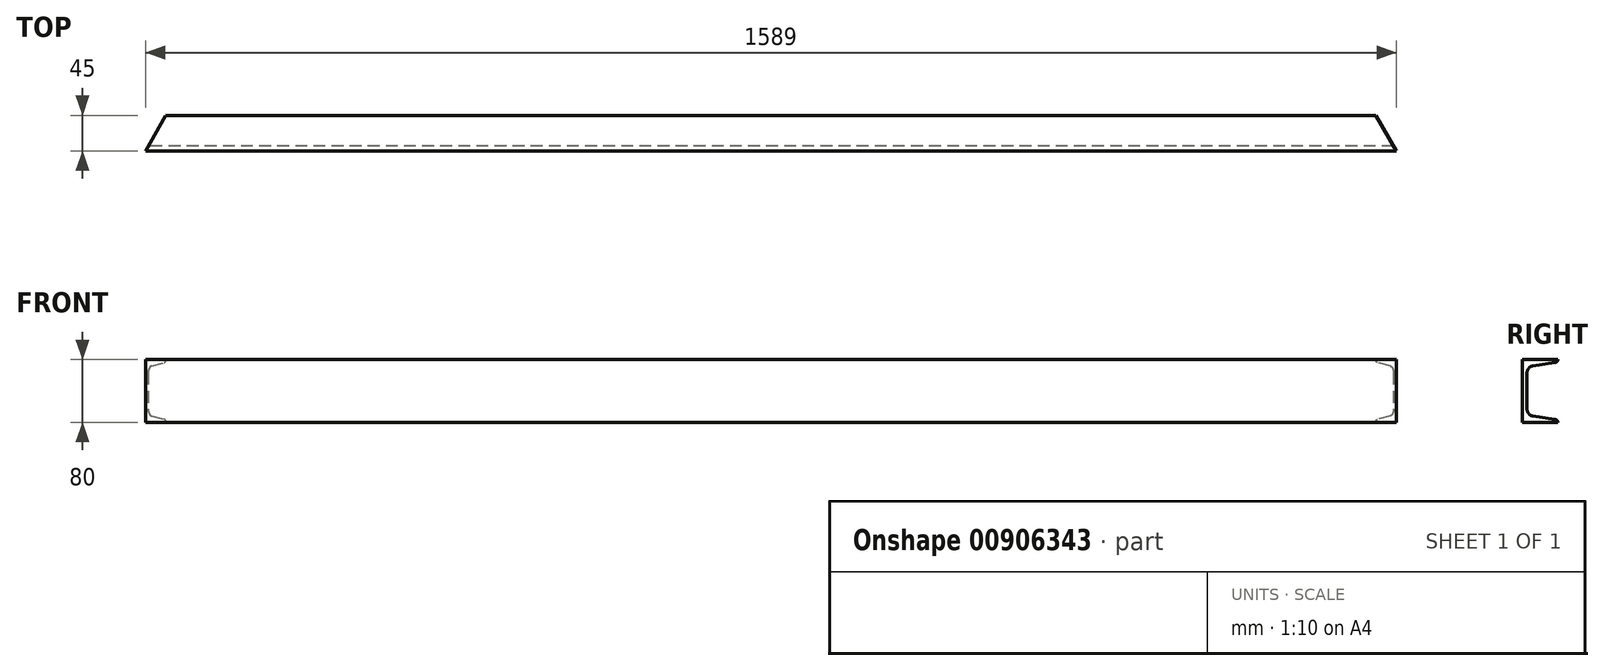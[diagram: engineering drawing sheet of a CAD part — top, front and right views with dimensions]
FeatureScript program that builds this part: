
annotation { "Feature Type Name" : "Feature", "Feature Type Description" : "" }
export const myFeature = defineFeature(function(context is Context, id is Id, definition is map)
    precondition{}
    {
        {
            var Q0;
            Q0=qCreatedBy(makeId("Top.planeOp"),FACE);
            var sketch = newSketch(context, id + "F0", { "sketchPlane" : qUnion([Q0])});
            skLineSegment(sketch, "E0", {"start": v(-794.5, 0) * mm, "end": v(794.5, 0) * mm});
            skLineSegment(sketch, "E1", {"start": v(794.5, 0) * mm, "end": v(768.52, 45) * mm});
            skLineSegment(sketch, "E2", {"start": v(768.52, 45) * mm, "end": v(-768.52, 45) * mm});
            skLineSegment(sketch, "E3", {"start": v(-768.52, 45) * mm, "end": v(-794.5, 0) * mm});
            skLineSegment(sketch, "E4", {"start": v(0, 220.63) * mm, "end": v(0, 0) * mm, "construction": true});
            skSolve(sketch);
        }
        {
            var Q0;
            Q0=qCreatedBy(makeId("Right.planeOp"),FACE);
            var sketch = newSketch(context, id + "F1", { "sketchPlane" : qUnion([Q0])});
            skLineSegment(sketch, "E5", {"start": v(0, 40) * mm, "end": v(0, 80) * mm});
            skLineSegment(sketch, "E6", {"start": v(0, 80) * mm, "end": v(45, 80) * mm});
            skPoint(sketch, "E7.startSnap0", {"position": v(0, 40) * mm});
            skLineSegment(sketch, "E8", {"start": v(0, 40) * mm, "end": v(15, 40) * mm});
            skLineSegment(sketch, "E9", {"start": v(15, 40) * mm, "end": v(15, 63) * mm, "construction": true});
            skLineSegment(sketch, "E10", {"start": v(15, 40) * mm, "end": v(15, 17) * mm, "construction": true});
            skLineSegment(sketch, "E11", {"start": v(6, 63) * mm, "end": v(6, 40) * mm});
            skArc(sketch, "E12", {"start": v(13.68, 71.9) * mm, "mid": v(8.19, 68.88) * mm, "end": v(6, 63) * mm});
            skArc(sketch, "E13", {"start": v(41.59, 76.04) * mm, "mid": v(44.03, 77.39) * mm, "end": v(45, 80) * mm});
            skLineSegment(sketch, "E14", {"start": v(13.68, 71.9) * mm, "end": v(41.59, 76.04) * mm});
            skArc(sketch, "E15.MirrorCS", {"start": v(13.68, 8.1) * mm, "mid": v(8.19, 11.12) * mm, "end": v(6, 17) * mm});
            skLineSegment(sketch, "E16.MirrorCS", {"start": v(0, 40) * mm, "end": v(0, 0) * mm});
            skLineSegment(sketch, "E17.MirrorCS", {"start": v(0, 0) * mm, "end": v(45, 0) * mm});
            skLineSegment(sketch, "E18.MirrorCS", {"start": v(6, 17) * mm, "end": v(6, 40) * mm});
            skArc(sketch, "E19.MirrorCS", {"start": v(41.59, 3.96) * mm, "mid": v(44.03, 2.61) * mm, "end": v(45, 0) * mm});
            skLineSegment(sketch, "E20.MirrorCS", {"start": v(13.68, 8.1) * mm, "end": v(41.59, 3.96) * mm});
            skSolve(sketch);
        }
        {
            var Q0;
            Q0 = qSketchRegion(id + "F1", true);
            extrude(context, id + "F2", {"entities" : qUnion([Q0]), "endBound" : BoundingType.SYMMETRIC, "depth" : 1589 * mm, "offsetDistance" : 25 * mm});
        }
        {
            var Q0;
            Q0=makeQuery(id+"F2.opExtrude","SWEPT_FACE",FACE,{"disambiguationData":[OSD([sQuery(id+"F1.wireOp",EDGE,"E6")])]});
            var sketch = newSketch(context, id + "F3", { "sketchPlane" : qUnion([Q0])});
            skLineSegment(sketch, "E21", {"start": v(-794.5, 45) * mm, "end": v(-794.5, 0) * mm});
            skLineSegment(sketch, "E22", {"start": v(-794.5, 0) * mm, "end": v(-768.52, 45) * mm});
            skLineSegment(sketch, "E23", {"start": v(-768.52, 45) * mm, "end": v(-794.5, 45) * mm});
            skLineSegment(sketch, "E24.MirrorCS", {"start": v(768.52, 45) * mm, "end": v(794.5, 45) * mm});
            skLineSegment(sketch, "E25.MirrorCS", {"start": v(794.5, 45) * mm, "end": v(794.5, 0) * mm});
            skLineSegment(sketch, "E26.MirrorCS", {"start": v(794.5, 0) * mm, "end": v(768.52, 45) * mm});
            skSolve(sketch);
        }
        {
            var Q0;
            Q0 = qSketchRegion(id + "F3", true);
            var Q1;
            Q1=makeQuery(id+"F2.opExtrude","SWEPT_FACE",FACE,{"disambiguationData":[OSD([sQuery(id+"F1.wireOp",EDGE,"E17.MirrorCS")])]});
            extrude(context, id + "F4", {"entities" : qUnion([Q0]), "operationType" : NewBodyOperationType.REMOVE, "endBound" : BoundingType.UP_TO_SURFACE, "oppositeDirection" : true, "depth" : 25 * mm, "endBoundEntityFace" : qUnion([Q1]), "offsetDistance" : 25 * mm});
        }
    });
